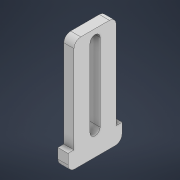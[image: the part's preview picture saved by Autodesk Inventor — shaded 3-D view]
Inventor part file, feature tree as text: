
AUTODESK INVENTOR PART (.ipt)
format: ipt  version: 2021 (Build 250183000, 183)  size: 125,440 bytes
history: native  units: mm
features: extrude x1, sketch x1
ambient origin geometry x8: Origin, YZ Plane, XZ Plane, XY Plane, X Axis, Y Axis, Z Axis, Center Point
bodies: Body1 (feature_tree)
feature tree (2):
  extrude  "Extrusion3"  Depth=5.0mm
  sketch  "Sketch1"  dims[d1=16.0mm d2=6.0mm d3=1.75mm d5=2.0mm d14=1.75mm d18=3.0mm d19=3.0mm d21=2.0mm d22=3.0mm d23=0.0mm d24=28.0mm d25=2.0mm d26=5.0mm]
